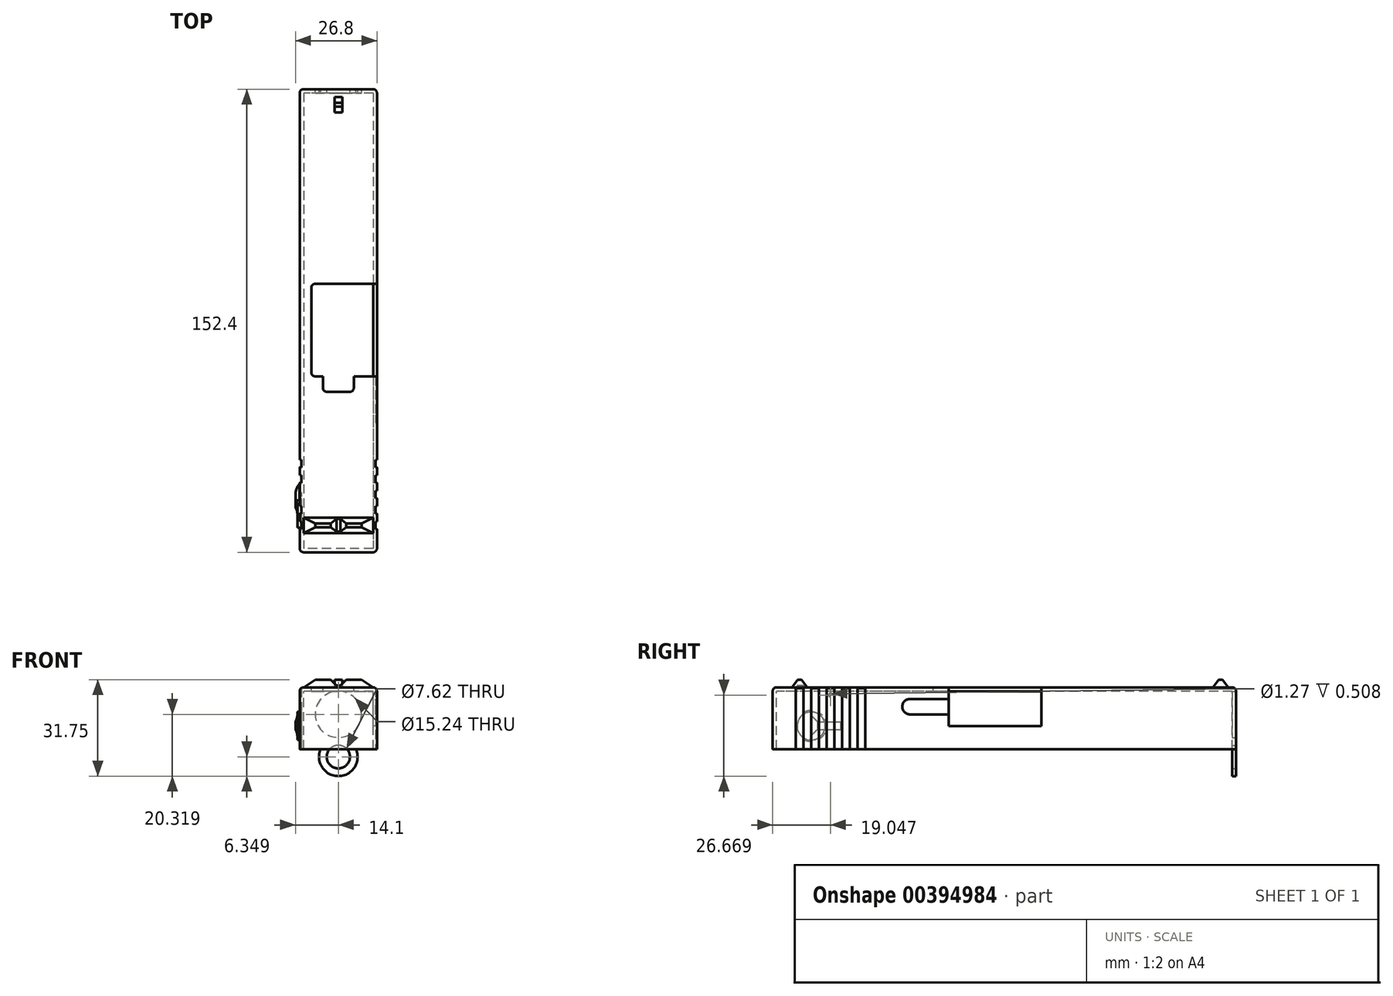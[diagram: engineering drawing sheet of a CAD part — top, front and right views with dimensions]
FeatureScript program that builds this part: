
annotation { "Feature Type Name" : "Feature", "Feature Type Description" : "" }
export const myFeature = defineFeature(function(context is Context, id is Id, definition is map)
    precondition{}
    {
        {
            var Q0;
            Q0=qCreatedBy(makeId("Right.planeOp"),FACE);
            var sketch = newSketch(context, id + "F0", { "sketchPlane" : qUnion([Q0])});
            skLineSegment(sketch, "E0.bottom", {"start": v(79.29, -14.73) * mm, "end": v(-73.11, -14.73) * mm});
            skLineSegment(sketch, "E0.top", {"start": v(79.29, 5.59) * mm, "end": v(-73.11, 5.59) * mm});
            skLineSegment(sketch, "E0.left", {"start": v(79.29, -14.73) * mm, "end": v(79.29, 5.59) * mm});
            skLineSegment(sketch, "E0.right", {"start": v(-73.11, -14.73) * mm, "end": v(-73.11, 5.59) * mm});
            skSolve(sketch);
        }
        {
            var Q0;
            Q0=makeQuery(id+"F0.imprint","IMPRINT",FACE,{"disambiguationData":[TD([[makeQuery(id+"F0.imprint","IMPRINT",EDGE,{"derivedFrom":sQuery(id+"F0.wireOp",EDGE,"E0.bottom")}),-1.0]])]});
            extrude(context, id + "F1", {"entities" : qUnion([Q0]), "depth" : 25.4 * mm});
        }
        {
            var Q0;
            Q0=makeQuery(id+"F1.opExtrude","SWEPT_FACE",FACE,{"disambiguationData":[OSD([sQuery(id+"F0.wireOp",EDGE,"E0.bottom")])]});
            shell(context, id + "F2", {"entities" : qUnion([Q0]), "thickness" : 1.27 * mm});
        }
        {
            var Q0;
            Q0=makeQuery(id+"F1.opExtrude","SWEPT_FACE",FACE,{"disambiguationData":[OSD([sQuery(id+"F0.wireOp",EDGE,"E0.left")])]});
            var sketch = newSketch(context, id + "F3", { "sketchPlane" : qUnion([Q0])});
            skCircle(sketch, "E1", {"center": v(-12.7, -3.3) * mm, "radius": 7.62 * mm});
            skCircle(sketch, "E2", {"center": v(-12.7, -17.27) * mm, "radius": 3.81 * mm});
            skPoint(sketch, "E2.centerSnap0", {"position": v(-12.7, -14.73) * mm});
            skSolve(sketch);
        }
        {
            var Q0;
            Q0=makeQuery(id+"F1.opExtrude","SWEPT_FACE",FACE,{"disambiguationData":[OSD([sQuery(id+"F0.wireOp",EDGE,"E0.left")])]});
            var sketch = newSketch(context, id + "F4", { "sketchPlane" : qUnion([Q0])});
            skArc(sketch, "E3", {"start": v(-18.52, -14.73) * mm, "mid": v(-12.7, -23.62) * mm, "end": v(-6.88, -14.73) * mm});
            skLineSegment(sketch, "E4", {"start": v(-18.52, -14.73) * mm, "end": v(-6.88, -14.73) * mm});
            skSolve(sketch);
        }
        {
            var Q0;
            Q0=makeQuery(id+"F4.imprint","IMPRINT",FACE,{"disambiguationData":[TD([[makeQuery(id+"F4.imprint","IMPRINT",EDGE,{"derivedFrom":sQuery(id+"F4.wireOp",EDGE,"E3")}),1.0]])]});
            extrude(context, id + "F5", {"entities" : qUnion([Q0]), "operationType" : NewBodyOperationType.ADD, "oppositeDirection" : true, "depth" : 1.27 * mm});
        }
        {
            var Q0;
            Q0=makeQuery(id+"F3.imprint","IMPRINT",FACE,{"disambiguationData":[TD([[makeQuery(id+"F3.imprint","IMPRINT",EDGE,{"derivedFrom":sQuery(id+"F3.wireOp",EDGE,"E1")}),1.0]])]});
            var Q1;
            {var subQ0=sQuery(id+"F3.wireOp",EDGE,"E2");var subQ1=makeQuery(id+"F1.opExtrude","SWEPT_EDGE",EDGE,{"disambiguationData":[OSD([sQuery(id+"F0.wireOp",EDGE,"E0.bottom"),sQuery(id+"F0.wireOp",EDGE,"E0.left")])]});var subQ2=makeQuery(id+"F3.imprint","INTERSECT",VERTEX,{"disambiguationData":[OD(0.0)],"derivedFrom":[subQ1,subQ0]});Q1=makeQuery(id+"F3.imprint","IMPRINT",FACE,{"disambiguationData":[TD([[makeQuery(id+"F3.imprint","IMPRINT",EDGE,{"disambiguationData":[TD([[subQ2,1.0]])],"derivedFrom":subQ0}),1.0]])]});}
            var Q2;
            {var subQ0=sQuery(id+"F3.wireOp",EDGE,"E2");var subQ1=makeQuery(id+"F1.opExtrude","SWEPT_EDGE",EDGE,{"disambiguationData":[OSD([sQuery(id+"F0.wireOp",EDGE,"E0.bottom"),sQuery(id+"F0.wireOp",EDGE,"E0.left")])]});var subQ2=makeQuery(id+"F3.imprint","INTERSECT",VERTEX,{"disambiguationData":[OD(0.0)],"derivedFrom":[subQ1,subQ0]});Q2=makeQuery(id+"F3.imprint","IMPRINT",FACE,{"disambiguationData":[TD([[makeQuery(id+"F3.imprint","IMPRINT",EDGE,{"disambiguationData":[TD([[subQ2,-1.0]])],"derivedFrom":subQ0}),1.0]])]});}
            extrude(context, id + "F6", {"entities" : qUnion([Q0, Q1, Q2]), "operationType" : NewBodyOperationType.REMOVE, "oppositeDirection" : true, "depth" : 25.4 * mm});
        }
        {
            var Q0;
            Q0=makeQuery(id+"F1.opExtrude","SWEPT_FACE",FACE,{"disambiguationData":[OSD([sQuery(id+"F0.wireOp",EDGE,"E0.top")])]});
            var sketch = newSketch(context, id + "F7", { "sketchPlane" : qUnion([Q0])});
            skLineSegment(sketch, "E5.bottom", {"start": v(25.4, 15.24) * mm, "end": v(3.8, 15.24) * mm});
            skLineSegment(sketch, "E5.top", {"start": v(25.4, -15.24) * mm, "end": v(17.78, -15.24) * mm});
            skLineSegment(sketch, "E5.left", {"start": v(25.4, 15.24) * mm, "end": v(25.4, -15.24) * mm});
            skLineSegment(sketch, "E5.right", {"start": v(3.8, 15.24) * mm, "end": v(3.81, -15.24) * mm});
            skLineSegment(sketch, "E6.top", {"start": v(7.62, -20.32) * mm, "end": v(17.78, -20.32) * mm});
            skLineSegment(sketch, "E6.left", {"start": v(7.62, -15.24) * mm, "end": v(7.62, -20.32) * mm});
            skLineSegment(sketch, "E6.right", {"start": v(17.78, -15.24) * mm, "end": v(17.78, -20.32) * mm});
            skLineSegment(sketch, "E7.trimOffspring", {"start": v(7.62, -15.24) * mm, "end": v(3.81, -15.24) * mm});
            skSolve(sketch);
        }
        {
            var Q0;
            Q0=makeQuery(id+"F7.imprint","IMPRINT",FACE,{"disambiguationData":[TD([[makeQuery(id+"F7.imprint","IMPRINT",EDGE,{"derivedFrom":sQuery(id+"F7.wireOp",EDGE,"E5.bottom")}),1.0]])]});
            extrude(context, id + "F8", {"entities" : qUnion([Q0]), "operationType" : NewBodyOperationType.REMOVE, "oppositeDirection" : true, "depth" : 12.7 * mm});
        }
        {
            var Q0;
            Q0=makeQuery(id+"F1.opExtrude","CAP_FACE",FACE,{"disambiguationData":[OSD([sQuery(id+"F0.wireOp",EDGE,"E0.bottom"),sQuery(id+"F0.wireOp",EDGE,"E0.top"),sQuery(id+"F0.wireOp",EDGE,"E0.left"),sQuery(id+"F0.wireOp",EDGE,"E0.right")])],"isStart":false});
            var sketch = newSketch(context, id + "F9", { "sketchPlane" : qUnion([Q0])});
            skLineSegment(sketch, "E8.bottom", {"start": v(-15.24, 1.78) * mm, "end": v(-27.94, 1.78) * mm});
            skLineSegment(sketch, "E8.top", {"start": v(-15.24, -3.3) * mm, "end": v(-27.94, -3.3) * mm});
            skLineSegment(sketch, "E8.left", {"start": v(-15.24, 1.78) * mm, "end": v(-15.24, -3.3) * mm});
            skArc(sketch, "E9", {"start": v(-27.94, 1.78) * mm, "mid": v(-30.48, -0.76) * mm, "end": v(-27.94, -3.3) * mm});
            skSolve(sketch);
        }
        {
            var Q0;
            Q0=makeQuery(id+"F9.imprint","IMPRINT",FACE,{"disambiguationData":[TD([[makeQuery(id+"F9.imprint","IMPRINT",EDGE,{"derivedFrom":sQuery(id+"F9.wireOp",EDGE,"E8.bottom")}),1.0]])]});
            extrude(context, id + "F10", {"entities" : qUnion([Q0]), "operationType" : NewBodyOperationType.REMOVE, "oppositeDirection" : true, "depth" : 0.5 * mm});
        }
        {
            var Q0;
            Q0=makeQuery(id+"F1.opExtrude","CAP_FACE",FACE,{"disambiguationData":[OSD([sQuery(id+"F0.wireOp",EDGE,"E0.bottom"),sQuery(id+"F0.wireOp",EDGE,"E0.top"),sQuery(id+"F0.wireOp",EDGE,"E0.left"),sQuery(id+"F0.wireOp",EDGE,"E0.right")])],"isStart":false});
            var sketch = newSketch(context, id + "F11", { "sketchPlane" : qUnion([Q0])});
            skLineSegment(sketch, "E10.bottom", {"start": v(-65.5, 5.59) * mm, "end": v(-62.95, 5.59) * mm});
            skLineSegment(sketch, "E10.top", {"start": v(-65.5, -14.73) * mm, "end": v(-62.95, -14.73) * mm});
            skLineSegment(sketch, "E10.left", {"start": v(-65.5, 5.59) * mm, "end": v(-65.5, -14.73) * mm});
            skLineSegment(sketch, "E10.right", {"start": v(-62.95, 5.59) * mm, "end": v(-62.95, -14.73) * mm});
            skLineSegment(sketch, "E11.bottom", {"start": v(-60.41, 5.59) * mm, "end": v(-57.87, 5.59) * mm});
            skLineSegment(sketch, "E11.top", {"start": v(-60.41, -14.73) * mm, "end": v(-57.87, -14.73) * mm});
            skLineSegment(sketch, "E11.left", {"start": v(-60.41, 5.59) * mm, "end": v(-60.41, -14.73) * mm});
            skLineSegment(sketch, "E11.right", {"start": v(-57.87, 5.59) * mm, "end": v(-57.87, -14.73) * mm});
            skLineSegment(sketch, "E12.bottom", {"start": v(-55.33, 5.59) * mm, "end": v(-52.8, 5.59) * mm});
            skLineSegment(sketch, "E12.top", {"start": v(-55.33, -14.73) * mm, "end": v(-52.8, -14.73) * mm});
            skLineSegment(sketch, "E12.left", {"start": v(-55.33, 5.59) * mm, "end": v(-55.33, -14.73) * mm});
            skLineSegment(sketch, "E12.right", {"start": v(-52.8, 5.59) * mm, "end": v(-52.8, -14.73) * mm});
            skLineSegment(sketch, "E13.bottom", {"start": v(-50.25, 5.59) * mm, "end": v(-47.71, 5.59) * mm});
            skLineSegment(sketch, "E13.top", {"start": v(-50.25, -14.73) * mm, "end": v(-47.71, -14.73) * mm});
            skLineSegment(sketch, "E13.left", {"start": v(-50.25, 5.59) * mm, "end": v(-50.25, -14.73) * mm});
            skLineSegment(sketch, "E13.right", {"start": v(-47.71, 5.59) * mm, "end": v(-47.71, -14.73) * mm});
            skLineSegment(sketch, "E14.bottom", {"start": v(-45.17, 5.59) * mm, "end": v(-42.63, 5.59) * mm});
            skLineSegment(sketch, "E14.top", {"start": v(-45.17, -14.73) * mm, "end": v(-42.63, -14.73) * mm});
            skLineSegment(sketch, "E14.left", {"start": v(-45.17, 5.59) * mm, "end": v(-45.17, -14.73) * mm});
            skLineSegment(sketch, "E14.right", {"start": v(-42.63, 5.59) * mm, "end": v(-42.63, -14.73) * mm});
            skSolve(sketch);
        }
        {
            var Q0;
            Q0 = qSketchRegion(id + "F11", true);
            extrude(context, id + "F12", {"entities" : qUnion([Q0]), "operationType" : NewBodyOperationType.REMOVE, "oppositeDirection" : true, "depth" : 0.5 * mm});
        }
        {
            var Q0;
            Q0=makeQuery(id+"F1.opExtrude","CAP_FACE",FACE,{"disambiguationData":[OSD([sQuery(id+"F0.wireOp",EDGE,"E0.bottom"),sQuery(id+"F0.wireOp",EDGE,"E0.top"),sQuery(id+"F0.wireOp",EDGE,"E0.left"),sQuery(id+"F0.wireOp",EDGE,"E0.right")])],"isStart":true});
            var sketch = newSketch(context, id + "F13", { "sketchPlane" : qUnion([Q0])});
            skLineSegment(sketch, "E15.bottom", {"start": v(65.5, 5.59) * mm, "end": v(62.95, 5.59) * mm});
            skLineSegment(sketch, "E15.top", {"start": v(65.5, -14.73) * mm, "end": v(62.95, -14.73) * mm});
            skLineSegment(sketch, "E15.left", {"start": v(65.5, 5.59) * mm, "end": v(65.5, -14.73) * mm});
            skLineSegment(sketch, "E15.right", {"start": v(62.95, 5.59) * mm, "end": v(62.95, -2.71) * mm});
            skLineSegment(sketch, "E16.bottom", {"start": v(60.41, 5.59) * mm, "end": v(57.87, 5.59) * mm});
            skLineSegment(sketch, "E16.top", {"start": v(60.41, -14.73) * mm, "end": v(57.87, -14.73) * mm});
            skLineSegment(sketch, "E16.left", {"start": v(60.41, 5.59) * mm, "end": v(60.41, -2.03) * mm});
            skLineSegment(sketch, "E16.right", {"start": v(57.87, 5.59) * mm, "end": v(57.87, -2.71) * mm});
            skLineSegment(sketch, "E17.bottom", {"start": v(50.25, 5.59) * mm, "end": v(47.71, 5.59) * mm});
            skLineSegment(sketch, "E17.top", {"start": v(50.25, -14.73) * mm, "end": v(47.71, -14.73) * mm});
            skLineSegment(sketch, "E17.left", {"start": v(50.25, 5.59) * mm, "end": v(50.25, -14.73) * mm});
            skLineSegment(sketch, "E17.right", {"start": v(47.71, 5.59) * mm, "end": v(47.71, -14.73) * mm});
            skLineSegment(sketch, "E18.bottom", {"start": v(45.17, 5.59) * mm, "end": v(42.63, 5.59) * mm});
            skLineSegment(sketch, "E18.top", {"start": v(45.17, -14.73) * mm, "end": v(42.63, -14.73) * mm});
            skLineSegment(sketch, "E18.left", {"start": v(45.17, 5.59) * mm, "end": v(45.17, -14.73) * mm});
            skLineSegment(sketch, "E18.right", {"start": v(42.63, 5.59) * mm, "end": v(42.63, -14.73) * mm});
            skArc(sketch, "E19", {"start": v(57.87, -2.71) * mm, "mid": v(55.33, -7.11) * mm, "end": v(57.87, -11.51) * mm});
            skLineSegment(sketch, "E20.trimOffspring", {"start": v(62.95, -11.51) * mm, "end": v(62.95, -14.73) * mm});
            skLineSegment(sketch, "E21.trimOffspring", {"start": v(60.41, -12.2) * mm, "end": v(60.41, -14.73) * mm});
            skLineSegment(sketch, "E22.trimOffspring", {"start": v(57.87, -11.51) * mm, "end": v(57.87, -14.73) * mm});
            skArc(sketch, "E23.trimOffspring", {"start": v(60.41, -12.2) * mm, "mid": v(61.73, -12.02) * mm, "end": v(62.95, -11.51) * mm});
            skArc(sketch, "E24.trimOffspring", {"start": v(62.95, -2.71) * mm, "mid": v(61.73, -2.2) * mm, "end": v(60.41, -2.03) * mm});
            skCircle(sketch, "E25", {"center": v(54.06, 3.05) * mm, "radius": 0.64 * mm});
            skSolve(sketch);
        }
        {
            var Q0;
            Q0 = qSketchRegion(id + "F13", true);
            extrude(context, id + "F14", {"entities" : qUnion([Q0]), "operationType" : NewBodyOperationType.REMOVE, "oppositeDirection" : true, "depth" : 0.5 * mm});
        }
        {
            var Q0;
            {var subQ0=sQuery(id+"F0.wireOp",EDGE,"E0.left");var subQ1=sQuery(id+"F0.wireOp",EDGE,"E0.top");Q0=makeQuery(id+"F8.boolean.opBoolean","SPLIT",EDGE,{"disambiguationData":[TD([makeQuery(id+"F1.opExtrude","SWEPT_FACE",FACE,{"disambiguationData":[OSD([subQ0])]})])],"derivedFrom":makeQuery(id+"F1.opExtrude","CAP_EDGE",EDGE,{"disambiguationData":[OSD([subQ1])],"isStart":false})});}
            var Q1;
            {var subQ0=sQuery(id+"F0.wireOp",EDGE,"E0.right");var subQ1=sQuery(id+"F0.wireOp",EDGE,"E0.top");var subQ4=makeQuery(id+"F8.opExtrude","SWEPT_FACE",FACE,{"disambiguationData":[OSD([sQuery(id+"F7.wireOp",EDGE,"E5.top")])]});Q1=makeQuery(id+"F12.boolean.opBoolean","SPLIT",EDGE,{"disambiguationData":[TD([makeQuery(id+"F8.boolean.opBoolean","COPY",FACE,{"derivedFrom":subQ4})])],"derivedFrom":makeQuery(id+"F8.boolean.opBoolean","SPLIT",EDGE,{"disambiguationData":[TD([makeQuery(id+"F1.opExtrude","SWEPT_FACE",FACE,{"disambiguationData":[OSD([subQ0])]})])],"derivedFrom":makeQuery(id+"F1.opExtrude","CAP_EDGE",EDGE,{"disambiguationData":[OSD([subQ1])],"isStart":false})})});}
            var Q2;
            Q2=makeQuery(id+"F1.opExtrude","SWEPT_EDGE",EDGE,{"disambiguationData":[OSD([sQuery(id+"F0.wireOp",EDGE,"E0.top"),sQuery(id+"F0.wireOp",EDGE,"E0.right")])]});
            var Q3;
            {var subQ0=sQuery(id+"F0.wireOp",EDGE,"E0.right");var subQ1=sQuery(id+"F0.wireOp",EDGE,"E0.top");var subQ4=makeQuery(id+"F1.opExtrude","SWEPT_FACE",FACE,{"disambiguationData":[OSD([subQ0])]});Q3=makeQuery(id+"F12.boolean.opBoolean","SPLIT",EDGE,{"disambiguationData":[TD([subQ4])],"derivedFrom":makeQuery(id+"F8.boolean.opBoolean","SPLIT",EDGE,{"disambiguationData":[TD([subQ4])],"derivedFrom":makeQuery(id+"F1.opExtrude","CAP_EDGE",EDGE,{"disambiguationData":[OSD([subQ1])],"isStart":false})})});}
            var Q4;
            {var subQ0=sQuery(id+"F0.wireOp",EDGE,"E0.right");var subQ1=sQuery(id+"F0.wireOp",EDGE,"E0.top");Q4=makeQuery(id+"F12.boolean.opBoolean","SPLIT",EDGE,{"disambiguationData":[TD([makeQuery(id+"F12.opExtrude","SWEPT_FACE",FACE,{"disambiguationData":[OSD([sQuery(id+"F11.wireOp",EDGE,"E13.right")])]})])],"derivedFrom":makeQuery(id+"F8.boolean.opBoolean","SPLIT",EDGE,{"disambiguationData":[TD([makeQuery(id+"F1.opExtrude","SWEPT_FACE",FACE,{"disambiguationData":[OSD([subQ0])]})])],"derivedFrom":makeQuery(id+"F1.opExtrude","CAP_EDGE",EDGE,{"disambiguationData":[OSD([subQ1])],"isStart":false})})});}
            var Q5;
            {var subQ0=sQuery(id+"F0.wireOp",EDGE,"E0.right");var subQ1=sQuery(id+"F0.wireOp",EDGE,"E0.top");Q5=makeQuery(id+"F12.boolean.opBoolean","SPLIT",EDGE,{"disambiguationData":[TD([makeQuery(id+"F12.opExtrude","SWEPT_FACE",FACE,{"disambiguationData":[OSD([sQuery(id+"F11.wireOp",EDGE,"E10.right")])]})])],"derivedFrom":makeQuery(id+"F8.boolean.opBoolean","SPLIT",EDGE,{"disambiguationData":[TD([makeQuery(id+"F1.opExtrude","SWEPT_FACE",FACE,{"disambiguationData":[OSD([subQ0])]})])],"derivedFrom":makeQuery(id+"F1.opExtrude","CAP_EDGE",EDGE,{"disambiguationData":[OSD([subQ1])],"isStart":false})})});}
            var Q6;
            {var subQ0=sQuery(id+"F0.wireOp",EDGE,"E0.right");var subQ1=sQuery(id+"F0.wireOp",EDGE,"E0.top");Q6=makeQuery(id+"F12.boolean.opBoolean","SPLIT",EDGE,{"disambiguationData":[TD([makeQuery(id+"F12.opExtrude","SWEPT_FACE",FACE,{"disambiguationData":[OSD([sQuery(id+"F11.wireOp",EDGE,"E11.right")])]})])],"derivedFrom":makeQuery(id+"F8.boolean.opBoolean","SPLIT",EDGE,{"disambiguationData":[TD([makeQuery(id+"F1.opExtrude","SWEPT_FACE",FACE,{"disambiguationData":[OSD([subQ0])]})])],"derivedFrom":makeQuery(id+"F1.opExtrude","CAP_EDGE",EDGE,{"disambiguationData":[OSD([subQ1])],"isStart":false})})});}
            var Q7;
            {var subQ0=sQuery(id+"F0.wireOp",EDGE,"E0.right");var subQ1=sQuery(id+"F0.wireOp",EDGE,"E0.top");Q7=makeQuery(id+"F12.boolean.opBoolean","SPLIT",EDGE,{"disambiguationData":[TD([makeQuery(id+"F12.opExtrude","SWEPT_FACE",FACE,{"disambiguationData":[OSD([sQuery(id+"F11.wireOp",EDGE,"E12.right")])]})])],"derivedFrom":makeQuery(id+"F8.boolean.opBoolean","SPLIT",EDGE,{"disambiguationData":[TD([makeQuery(id+"F1.opExtrude","SWEPT_FACE",FACE,{"disambiguationData":[OSD([subQ0])]})])],"derivedFrom":makeQuery(id+"F1.opExtrude","CAP_EDGE",EDGE,{"disambiguationData":[OSD([subQ1])],"isStart":false})})});}
            var Q8;
            Q8=makeQuery(id+"F1.opExtrude","CAP_EDGE",EDGE,{"disambiguationData":[OSD([sQuery(id+"F0.wireOp",EDGE,"E0.right")])],"isStart":false});
            var Q9;
            {var subQ0=sQuery(id+"F0.wireOp",EDGE,"E0.top");Q9=makeQuery(id+"F14.boolean.opBoolean","SPLIT",EDGE,{"disambiguationData":[TD([makeQuery(id+"F14.opExtrude","SWEPT_FACE",FACE,{"disambiguationData":[OSD([sQuery(id+"F13.wireOp",EDGE,"E15.right")])]})])],"derivedFrom":makeQuery(id+"F1.opExtrude","CAP_EDGE",EDGE,{"disambiguationData":[OSD([subQ0])],"isStart":true})});}
            var Q10;
            {var subQ0=sQuery(id+"F0.wireOp",EDGE,"E0.top");Q10=makeQuery(id+"F14.boolean.opBoolean","SPLIT",EDGE,{"disambiguationData":[TD([makeQuery(id+"F14.opExtrude","SWEPT_FACE",FACE,{"disambiguationData":[OSD([sQuery(id+"F13.wireOp",EDGE,"E16.right")])]})])],"derivedFrom":makeQuery(id+"F1.opExtrude","CAP_EDGE",EDGE,{"disambiguationData":[OSD([subQ0])],"isStart":true})});}
            var Q11;
            {var subQ0=sQuery(id+"F0.wireOp",EDGE,"E0.top");Q11=makeQuery(id+"F14.boolean.opBoolean","SPLIT",EDGE,{"disambiguationData":[TD([makeQuery(id+"F14.opExtrude","SWEPT_FACE",FACE,{"disambiguationData":[OSD([sQuery(id+"F13.wireOp",EDGE,"E17.right")])]})])],"derivedFrom":makeQuery(id+"F1.opExtrude","CAP_EDGE",EDGE,{"disambiguationData":[OSD([subQ0])],"isStart":true})});}
            var Q12;
            {var subQ0=sQuery(id+"F0.wireOp",EDGE,"E0.right");var subQ1=sQuery(id+"F0.wireOp",EDGE,"E0.top");Q12=makeQuery(id+"F14.boolean.opBoolean","SPLIT",EDGE,{"disambiguationData":[TD([makeQuery(id+"F1.opExtrude","SWEPT_FACE",FACE,{"disambiguationData":[OSD([subQ0])]})])],"derivedFrom":makeQuery(id+"F1.opExtrude","CAP_EDGE",EDGE,{"disambiguationData":[OSD([subQ1])],"isStart":true})});}
            var Q13;
            {var subQ0=sQuery(id+"F0.wireOp",EDGE,"E0.top");var subQ1=sQuery(id+"F0.wireOp",EDGE,"E0.left");Q13=makeQuery(id+"F14.boolean.opBoolean","SPLIT",EDGE,{"disambiguationData":[TD([makeQuery(id+"F1.opExtrude","SWEPT_FACE",FACE,{"disambiguationData":[OSD([subQ1])]})])],"derivedFrom":makeQuery(id+"F1.opExtrude","CAP_EDGE",EDGE,{"disambiguationData":[OSD([subQ0])],"isStart":true})});}
            var Q14;
            Q14=makeQuery(id+"F1.opExtrude","SWEPT_EDGE",EDGE,{"disambiguationData":[OSD([sQuery(id+"F0.wireOp",EDGE,"E0.top"),sQuery(id+"F0.wireOp",EDGE,"E0.left")])]});
            var Q15;
            Q15=makeQuery(id+"F1.opExtrude","CAP_EDGE",EDGE,{"disambiguationData":[OSD([sQuery(id+"F0.wireOp",EDGE,"E0.left")])],"isStart":false});
            var Q16;
            Q16=makeQuery(id+"F1.opExtrude","CAP_EDGE",EDGE,{"disambiguationData":[OSD([sQuery(id+"F0.wireOp",EDGE,"E0.left")])],"isStart":true});
            var Q17;
            Q17=makeQuery(id+"F1.opExtrude","CAP_EDGE",EDGE,{"disambiguationData":[OSD([sQuery(id+"F0.wireOp",EDGE,"E0.right")])],"isStart":true});
            fillet(context, id + "F15", {"entities" : qUnion([Q0, Q1, Q2, Q3, Q4, Q5, Q6, Q7, Q8, Q9, Q10, Q11, Q12, Q13, Q14, Q15, Q16, Q17]), "radius" : 1.27 * mm, "tangentPropagation" : true, "allowEdgeOverflow" : false});
        }
        {
            var Q0;
            Q0=qCreatedBy(makeId("Right.planeOp"),FACE);
            var sketch = newSketch(context, id + "F16", { "sketchPlane" : qUnion([Q0])});
            skLineSegment(sketch, "E26", {"start": v(76.75, 5.59) * mm, "end": v(74.84, 8.13) * mm});
            skLineSegment(sketch, "E27", {"start": v(74.84, 8.13) * mm, "end": v(73.57, 8.13) * mm});
            skLineSegment(sketch, "E28", {"start": v(73.57, 8.13) * mm, "end": v(71.67, 5.59) * mm});
            skLineSegment(sketch, "E29", {"start": v(76.75, 5.59) * mm, "end": v(71.67, 5.59) * mm});
            skSolve(sketch);
        }
        {
            var Q0;
            Q0 = qSketchRegion(id + "F16", true);
            extrude(context, id + "F17", {"entities" : qUnion([Q0]), "operationType" : NewBodyOperationType.ADD, "depth" : 25.4 * mm});
        }
        {
            var Q0;
            Q0=makeQuery(id+"F5.boolean.opBoolean","MERGE",FACE,{"derivedFrom":[makeQuery(id+"F1.opExtrude","SWEPT_FACE",FACE,{"disambiguationData":[OSD([sQuery(id+"F0.wireOp",EDGE,"E0.left")])]}),makeQuery(id+"F5.opExtrude","CAP_FACE",FACE,{"disambiguationData":[OSD([sQuery(id+"F4.wireOp",EDGE,"E3"),sQuery(id+"F4.wireOp",EDGE,"E4")])],"isStart":true})]});
            var sketch = newSketch(context, id + "F18", { "sketchPlane" : qUnion([Q0])});
            skLineSegment(sketch, "E30.bottom", {"start": v(-25.4, 8.13) * mm, "end": v(-13.97, 8.13) * mm});
            skLineSegment(sketch, "E30.top", {"start": v(-25.4, 5.59) * mm, "end": v(-13.97, 5.59) * mm});
            skLineSegment(sketch, "E30.left", {"start": v(-25.4, 8.13) * mm, "end": v(-25.4, 5.59) * mm});
            skLineSegment(sketch, "E30.right", {"start": v(-13.97, 8.13) * mm, "end": v(-13.97, 5.59) * mm});
            skLineSegment(sketch, "E31.bottom", {"start": v(0, 5.59) * mm, "end": v(-11.43, 5.59) * mm});
            skLineSegment(sketch, "E31.top", {"start": v(0, 8.13) * mm, "end": v(-11.43, 8.13) * mm});
            skLineSegment(sketch, "E31.left", {"start": v(0, 5.59) * mm, "end": v(0, 8.13) * mm});
            skLineSegment(sketch, "E31.right", {"start": v(-11.43, 5.59) * mm, "end": v(-11.43, 8.13) * mm});
            skSolve(sketch);
        }
        {
            var Q0;
            Q0 = qSketchRegion(id + "F18", true);
            extrude(context, id + "F19", {"entities" : qUnion([Q0]), "operationType" : NewBodyOperationType.REMOVE, "oppositeDirection" : true, "depth" : 25.4 * mm});
        }
        {
            var Q0;
            Q0=qCreatedBy(makeId("Right.planeOp"),FACE);
            var sketch = newSketch(context, id + "F20", { "sketchPlane" : qUnion([Q0])});
            skLineSegment(sketch, "E32", {"start": v(-61.68, 5.59) * mm, "end": v(-63.59, 8.13) * mm});
            skLineSegment(sketch, "E33", {"start": v(-63.59, 8.13) * mm, "end": v(-64.86, 8.13) * mm});
            skLineSegment(sketch, "E34", {"start": v(-64.86, 8.13) * mm, "end": v(-66.76, 5.59) * mm});
            skLineSegment(sketch, "E35", {"start": v(-61.68, 5.59) * mm, "end": v(-66.76, 5.59) * mm});
            skSolve(sketch);
        }
        {
            var Q0;
            Q0=makeQuery(id+"F20.imprint","IMPRINT",FACE,{"disambiguationData":[TD([[makeQuery(id+"F20.imprint","IMPRINT",EDGE,{"derivedFrom":sQuery(id+"F20.wireOp",EDGE,"E32")}),1.0]])]});
            extrude(context, id + "F21", {"entities" : qUnion([Q0]), "operationType" : NewBodyOperationType.ADD, "depth" : 25.4 * mm});
        }
        {
            var Q0;
            Q0=makeQuery(id+"F1.opExtrude","SWEPT_FACE",FACE,{"disambiguationData":[OSD([sQuery(id+"F0.wireOp",EDGE,"E0.right")])]});
            var sketch = newSketch(context, id + "F22", { "sketchPlane" : qUnion([Q0])});
            skLineSegment(sketch, "E36", {"start": v(0, 5.59) * mm, "end": v(0, 8.13) * mm});
            skLineSegment(sketch, "E37", {"start": v(0, 8.13) * mm, "end": v(5.08, 8.13) * mm});
            skLineSegment(sketch, "E38", {"start": v(5.08, 8.13) * mm, "end": v(1.27, 5.59) * mm});
            skLineSegment(sketch, "E39", {"start": v(1.27, 5.59) * mm, "end": v(0, 5.59) * mm});
            skLineSegment(sketch, "E40", {"start": v(20.32, 8.13) * mm, "end": v(25.4, 8.13) * mm});
            skLineSegment(sketch, "E41", {"start": v(25.4, 8.13) * mm, "end": v(25.4, 5.59) * mm});
            skLineSegment(sketch, "E42", {"start": v(25.4, 5.59) * mm, "end": v(24.13, 5.59) * mm});
            skLineSegment(sketch, "E43", {"start": v(24.13, 5.59) * mm, "end": v(20.32, 8.13) * mm});
            skLineSegment(sketch, "E44", {"start": v(10.16, 8.13) * mm, "end": v(12.07, 6.22) * mm});
            skLineSegment(sketch, "E45", {"start": v(12.07, 6.22) * mm, "end": v(13.34, 6.22) * mm});
            skLineSegment(sketch, "E46", {"start": v(13.34, 6.22) * mm, "end": v(15.24, 8.13) * mm});
            skLineSegment(sketch, "E47", {"start": v(10.16, 8.13) * mm, "end": v(15.24, 8.13) * mm});
            skSolve(sketch);
        }
        {
            var Q0;
            Q0 = qSketchRegion(id + "F22", true);
            extrude(context, id + "F23", {"entities" : qUnion([Q0]), "operationType" : NewBodyOperationType.REMOVE, "oppositeDirection" : true, "depth" : 25.4 * mm});
        }
        {
            var Q0;
            Q0=makeQuery(id+"F14.boolean.opBoolean","COPY",FACE,{"derivedFrom":makeQuery(id+"F14.opExtrude","CAP_FACE",FACE,{"disambiguationData":[OSD([sQuery(id+"F13.wireOp",EDGE,"E15.bottom"),sQuery(id+"F13.wireOp",EDGE,"E15.top"),sQuery(id+"F13.wireOp",EDGE,"E15.left"),sQuery(id+"F13.wireOp",EDGE,"E15.right"),sQuery(id+"F13.wireOp",EDGE,"E16.bottom"),sQuery(id+"F13.wireOp",EDGE,"E16.top"),sQuery(id+"F13.wireOp",EDGE,"E16.left"),sQuery(id+"F13.wireOp",EDGE,"E16.right"),sQuery(id+"F13.wireOp",EDGE,"E19"),sQuery(id+"F13.wireOp",EDGE,"E20.trimOffspring"),sQuery(id+"F13.wireOp",EDGE,"E21.trimOffspring"),sQuery(id+"F13.wireOp",EDGE,"E22.trimOffspring"),sQuery(id+"F13.wireOp",EDGE,"E23.trimOffspring"),sQuery(id+"F13.wireOp",EDGE,"E24.trimOffspring")])],"isStart":false})});
            var sketch = newSketch(context, id + "F24", { "sketchPlane" : qUnion([Q0])});
            skCircle(sketch, "E48", {"center": v(60.41, -7.11) * mm, "radius": 4.66 * mm});
            skSolve(sketch);
        }
        {
            var Q0;
            Q0=makeQuery(id+"F24.imprint","IMPRINT",FACE,{"disambiguationData":[TD([[makeQuery(id+"F24.imprint","IMPRINT",EDGE,{"derivedFrom":sQuery(id+"F24.wireOp",EDGE,"E48")}),1.0]])]});
            extrude(context, id + "F25", {"entities" : qUnion([Q0]), "depth" : 1.27 * mm, "hasDraft" : true, "draftAngle" : 3 * degree, "draftPullDirection" : true});
        }
        {
            var Q0;
            Q0=makeQuery(id+"F25.opExtrude","CAP_FACE",FACE,{"disambiguationData":[OSD([sQuery(id+"F24.wireOp",EDGE,"E48")])],"isStart":false});
            var sketch = newSketch(context, id + "F26", { "sketchPlane" : qUnion([Q0])});
            skLineSegment(sketch, "E49.bottom", {"start": v(58.36, -5.7) * mm, "end": v(50.74, -5.7) * mm});
            skLineSegment(sketch, "E49.top", {"start": v(58.36, -8.24) * mm, "end": v(50.74, -8.24) * mm});
            skLineSegment(sketch, "E49.left", {"start": v(58.36, -5.7) * mm, "end": v(58.36, -8.24) * mm});
            skLineSegment(sketch, "E49.right", {"start": v(50.74, -5.7) * mm, "end": v(50.74, -8.24) * mm});
            skSolve(sketch);
        }
        {
            var Q0;
            Q0 = qSketchRegion(id + "F26", true);
            extrude(context, id + "F27", {"entities" : qUnion([Q0]), "operationType" : NewBodyOperationType.ADD, "endBound" : BoundingType.SYMMETRIC, "depth" : 1.27 * mm});
        }
        {
            var Q0;
            Q0=makeQuery(id+"F27.boolean.opBoolean","INTERSECT",EDGE,{"derivedFrom":[makeQuery(id+"F25.opExtrude","CAP_FACE",FACE,{"disambiguationData":[OSD([sQuery(id+"F24.wireOp",EDGE,"E48")])],"isStart":false}),makeQuery(id+"F27.opExtrude","SWEPT_FACE",FACE,{"disambiguationData":[OSD([sQuery(id+"F26.wireOp",EDGE,"E49.left")])]})]});
            var Q1;
            Q1=makeQuery(id+"F27.boolean.opBoolean","INTERSECT",EDGE,{"derivedFrom":[makeQuery(id+"F25.opExtrude","CAP_FACE",FACE,{"disambiguationData":[OSD([sQuery(id+"F24.wireOp",EDGE,"E48")])],"isStart":false}),makeQuery(id+"F27.opExtrude","SWEPT_FACE",FACE,{"disambiguationData":[OSD([sQuery(id+"F26.wireOp",EDGE,"E49.bottom")])]})]});
            var Q2;
            Q2=makeQuery(id+"F27.boolean.opBoolean","INTERSECT",EDGE,{"derivedFrom":[makeQuery(id+"F25.opExtrude","CAP_FACE",FACE,{"disambiguationData":[OSD([sQuery(id+"F24.wireOp",EDGE,"E48")])],"isStart":false}),makeQuery(id+"F27.opExtrude","SWEPT_FACE",FACE,{"disambiguationData":[OSD([sQuery(id+"F26.wireOp",EDGE,"E49.top")])]})]});
            var Q3;
            Q3=makeQuery(id+"F27.opExtrude","CAP_EDGE",EDGE,{"disambiguationData":[OSD([sQuery(id+"F26.wireOp",EDGE,"E49.right")])],"isStart":false});
            fillet(context, id + "F28", {"entities" : qUnion([Q0, Q1, Q2, Q3]), "radius" : 5.08 * mm, "tangentPropagation" : true, "allowEdgeOverflow" : false});
        }
        {
            var Q0;
            Q0=makeQuery(id+"F8.boolean.opBoolean","COPY",EDGE,{"derivedFrom":makeQuery(id+"F8.opExtrude","SWEPT_EDGE",EDGE,{"disambiguationData":[OSD([sQuery(id+"F7.wireOp",EDGE,"E5.bottom"),sQuery(id+"F7.wireOp",EDGE,"E5.right")])]})});
            var Q1;
            Q1=makeQuery(id+"F8.boolean.opBoolean","COPY",EDGE,{"derivedFrom":makeQuery(id+"F8.opExtrude","SWEPT_EDGE",EDGE,{"disambiguationData":[OSD([sQuery(id+"F7.wireOp",EDGE,"E5.right"),sQuery(id+"F7.wireOp",EDGE,"E7.trimOffspring")])]})});
            var Q2;
            Q2=makeQuery(id+"F8.boolean.opBoolean","COPY",EDGE,{"derivedFrom":makeQuery(id+"F8.opExtrude","SWEPT_EDGE",EDGE,{"disambiguationData":[OSD([sQuery(id+"F7.wireOp",EDGE,"E6.top"),sQuery(id+"F7.wireOp",EDGE,"E6.left")])]})});
            var Q3;
            Q3=makeQuery(id+"F8.boolean.opBoolean","COPY",EDGE,{"derivedFrom":makeQuery(id+"F8.opExtrude","SWEPT_EDGE",EDGE,{"disambiguationData":[OSD([sQuery(id+"F7.wireOp",EDGE,"E6.top"),sQuery(id+"F7.wireOp",EDGE,"E6.right")])]})});
            fillet(context, id + "F29", {"entities" : qUnion([Q0, Q1, Q2, Q3]), "radius" : 1.27 * mm, "tangentPropagation" : true, "allowEdgeOverflow" : false});
        }
    });
